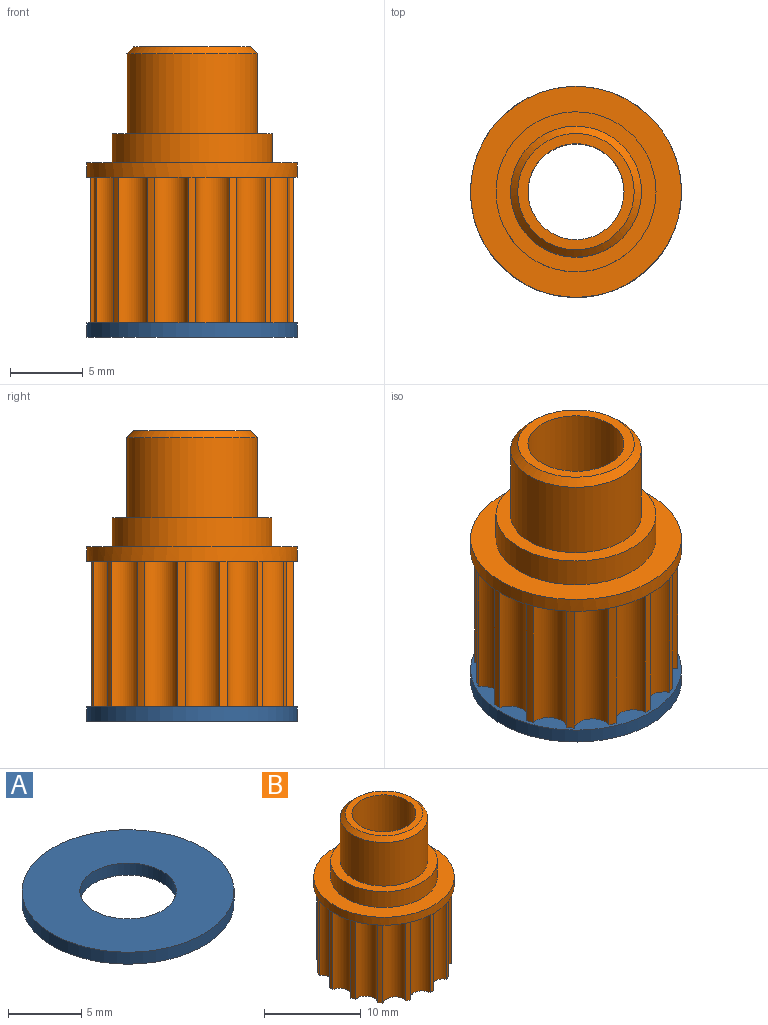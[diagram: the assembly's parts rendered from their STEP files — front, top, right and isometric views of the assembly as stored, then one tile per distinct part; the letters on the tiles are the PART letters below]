
ASSEMBLY  parts=2 mates=1
PART A: 4 faces, bbox 14.5x14.5x1 mm
  f0: cylinder r=7.25mm len=14.5mm, axis (0,0,-1), area 45.6mm2, adj f1,f2
  f1: plane 14.5x14.5mm, normal (0,0,1), area 130.9mm2, adj f0,f3
  f2: plane 14.5x14.5mm, normal (0,0,-1), area 130.9mm2, adj f0,f3
  f3: cylinder r=3.3mm len=6.6mm, axis (0,0,1), area 20.7mm2, adj f1,f2
PART B: 40 faces, bbox 14.5x14.5x19 mm
  f0: plane 13.97x13.9mm, normal (0,0,-1), area 93.5mm2, adj f1,f2,f3,f4,f5,f6,f7,f8
  f1: cylinder r=1.25mm len=10mm, axis (0,0,-1), area 32.1mm2, adj f0,f18,f20,f33
  f2: cylinder r=1.25mm len=10mm, axis (0,0,-1), area 32.1mm2, adj f0,f18,f32,f33
  f3: cylinder r=1.25mm len=10mm, axis (0,0,-1), area 32.1mm2, adj f0,f18,f31,f32
  f4: cylinder r=1.25mm len=10mm, axis (0,0,-1), area 32.1mm2, adj f0,f18,f30,f31
  f5: cylinder r=1.25mm len=10mm, axis (0,0,-1), area 32.1mm2, adj f0,f18,f29,f30
  f6: cylinder r=1.25mm len=10mm, axis (0,0,-1), area 32.1mm2, adj f0,f18,f28,f29
  f7: cylinder r=1.25mm len=10mm, axis (0,0,-1), area 32.1mm2, adj f0,f18,f27,f28
  f8: cylinder r=1.25mm len=10mm, axis (0,0,-1), area 32.1mm2, adj f0,f18,f26,f27
  f9: cylinder r=1.25mm len=10mm, axis (0,0,-1), area 32.1mm2, adj f0,f18,f25,f26
  f10: cylinder r=1.25mm len=10mm, axis (0,0,-1), area 32.1mm2, adj f0,f18,f24,f25
  f11: cylinder r=1.25mm len=10mm, axis (0,0,-1), area 32.1mm2, adj f0,f18,f23,f24
  f12: cylinder r=1.25mm len=10mm, axis (0,0,-1), area 32.1mm2, adj f0,f18,f22,f23
  f13: cylinder r=1.25mm len=10mm, axis (0,0,-1), area 32.1mm2, adj f0,f18,f21,f22
  f14: cylinder r=1.25mm len=10mm, axis (0,0,-1), area 32.1mm2, adj f0,f18,f19,f21
  f15: cylinder r=1.25mm len=10mm, axis (0,0,-1), area 32.1mm2, adj f0,f18,f19,f20
  f16: cylinder r=7.25mm len=14.5mm, axis (0,0,-1), area 45.6mm2, adj f17,f18
  f17: plane 14.5x14.5mm, normal (0,0,1), area 70.1mm2, adj f16,f34
  f18: plane 14.5x14.5mm, normal (0,0,-1), area 37.4mm2, adj f1,f2,f3,f4,f5,f6,f7,f8
  f19: cylinder r=7mm len=10mm, axis (0,0,-1), area 5.2mm2, adj f0,f14,f15,f18
  f20: cylinder r=7mm len=10mm, axis (0,0,-1), area 5.2mm2, adj f0,f1,f15,f18
  f21: cylinder r=7mm len=10mm, axis (0,0,-1), area 5.2mm2, adj f0,f13,f14,f18
  f22: cylinder r=7mm len=10mm, axis (0,0,-1), area 5.2mm2, adj f0,f12,f13,f18
  f23: cylinder r=7mm len=10mm, axis (0,0,-1), area 5.2mm2, adj f0,f11,f12,f18
  f24: cylinder r=7mm len=10mm, axis (0,0,-1), area 5.2mm2, adj f0,f10,f11,f18
  f25: cylinder r=7mm len=10mm, axis (0,0,-1), area 5.2mm2, adj f0,f9,f10,f18
  f26: cylinder r=7mm len=10mm, axis (0,0,-1), area 5.2mm2, adj f0,f8,f9,f18
  f27: cylinder r=7mm len=10mm, axis (0,0,-1), area 5.2mm2, adj f0,f7,f8,f18
  f28: cylinder r=7mm len=10mm, axis (0,0,-1), area 5.2mm2, adj f0,f6,f7,f18
  f29: cylinder r=7mm len=10mm, axis (0,0,-1), area 5.2mm2, adj f0,f5,f6,f18
  f30: cylinder r=7mm len=10mm, axis (0,0,-1), area 5.2mm2, adj f0,f4,f5,f18
  f31: cylinder r=7mm len=10mm, axis (0,0,-1), area 5.2mm2, adj f0,f3,f4,f18
  f32: cylinder r=7mm len=10mm, axis (0,0,-1), area 5.2mm2, adj f0,f2,f3,f18
  f33: cylinder r=7mm len=10mm, axis (0,0,-1), area 5.2mm2, adj f0,f1,f2,f18
  f34: cylinder r=5.5mm len=11mm, axis (0,0,-1), area 69.1mm2, adj f17,f35
  f35: plane 11x11mm, normal (0,0,1), area 31.4mm2, adj f34,f36
  f36: cylinder r=4.5mm len=9mm, axis (0,0,-1), area 155.5mm2, adj f35,f39
  f37: plane 8x8mm, normal (0,0,1), area 16.1mm2, adj f38,f39
  f38: cylinder r=3.3mm len=19mm, axis (0,0,1), area 394mm2, adj f0,f37
  f39: cone r=4mm half-angle=45deg, axis (0,0,-1), area 18.9mm2, adj f36,f37
PLACE A t=(-7.79,0.34,-3.75)mm
PLACE B t=(-7.79,0.34,-3.75)mm
MATE fastened B.f38 <-> A.f3  axis (0,0,-1) through (-7.79,0.34,-2.75)mm
